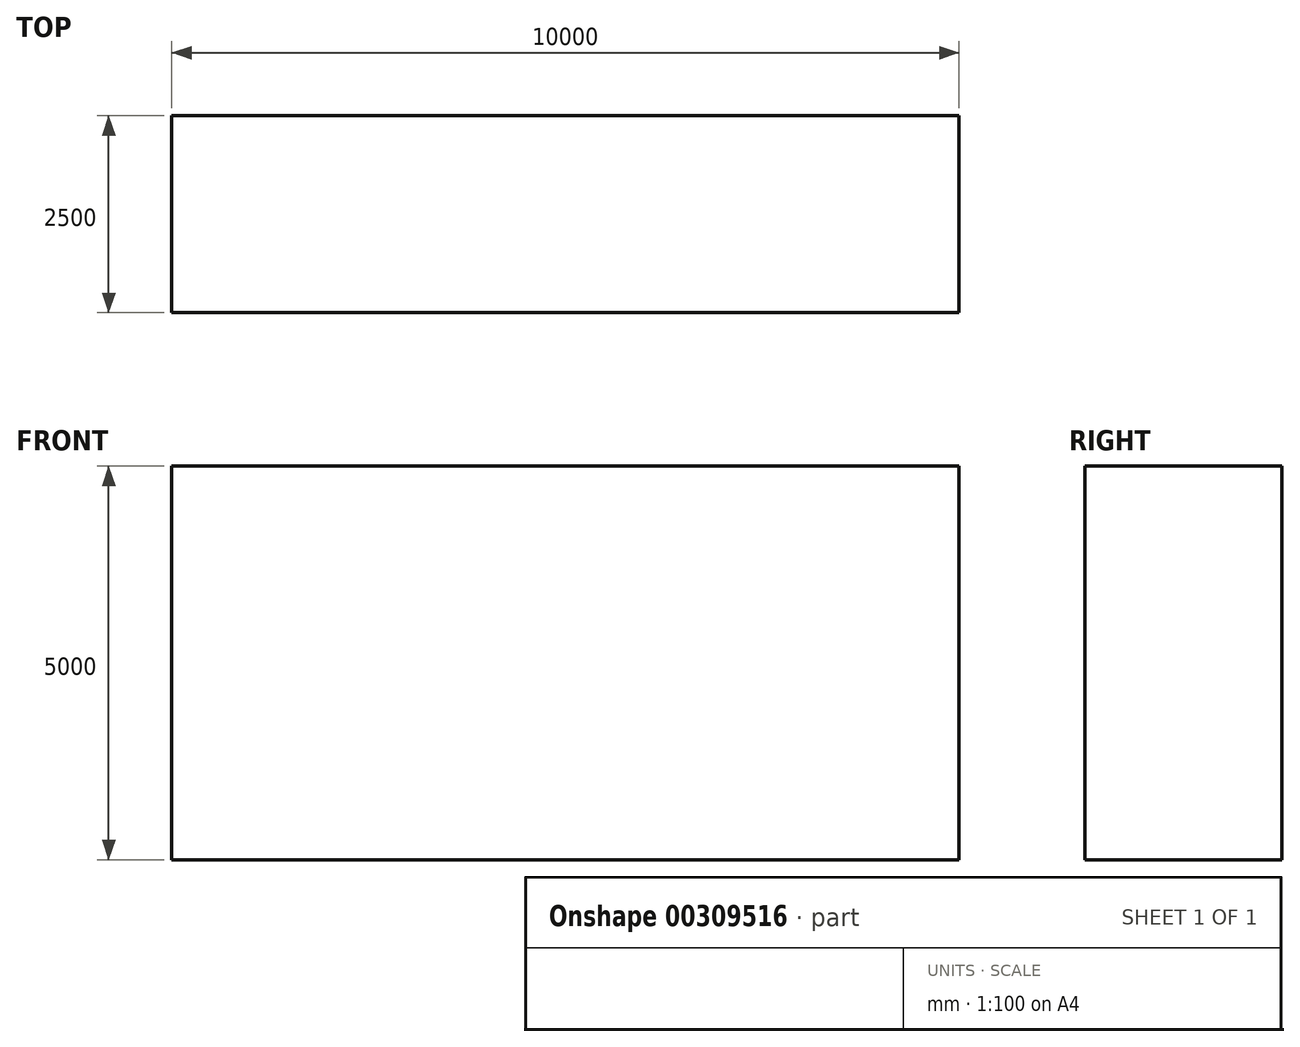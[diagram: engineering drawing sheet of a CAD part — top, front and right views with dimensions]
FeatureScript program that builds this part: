
annotation { "Feature Type Name" : "Feature", "Feature Type Description" : "" }
export const myFeature = defineFeature(function(context is Context, id is Id, definition is map)
    precondition{}
    {
        {
            var Q0;
            Q0=qCreatedBy(makeId("Front.planeOp"),FACE);
            var sketch = newSketch(context, id + "F0", { "sketchPlane" : qUnion([Q0])});
            skLineSegment(sketch, "E0.bottom", {"start": v(-5002.48, 2298.9) * mm, "end": v(4997.52, 2298.9) * mm});
            skLineSegment(sketch, "E0.top", {"start": v(-5002.48, -2701.1) * mm, "end": v(4997.52, -2701.1) * mm});
            skLineSegment(sketch, "E0.left", {"start": v(-5002.48, 2298.9) * mm, "end": v(-5002.48, -2701.1) * mm});
            skLineSegment(sketch, "E0.right", {"start": v(4997.52, 2298.9) * mm, "end": v(4997.52, -2701.1) * mm});
            skSolve(sketch);
        }
        {
            var Q0;
            Q0=makeQuery(id+"F0.imprint","IMPRINT",FACE,{"disambiguationData":[TD([[makeQuery(id+"F0.imprint","IMPRINT",EDGE,{"derivedFrom":sQuery(id+"F0.wireOp",EDGE,"E0.bottom")}),-1.0]])]});
            extrude(context, id + "F1", {"entities" : qUnion([Q0]), "depth" : 2500 * mm});
        }
    });
